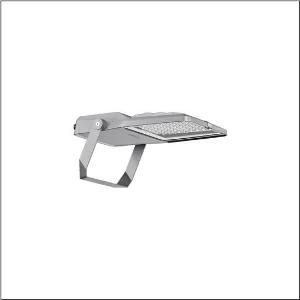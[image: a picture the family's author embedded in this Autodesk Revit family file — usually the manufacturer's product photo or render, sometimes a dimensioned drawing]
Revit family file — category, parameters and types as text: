
# Revit family: floodlight_fl_21_mini___pl64_5xa7776b2e1a_6c25
name_source: partatom
category: Lighting Fixtures
units: mm (PartAtom-declared; Revit-internal decimal feet)

## family parameters
Cut with Voids When Loaded = No
Host = Face
Light Source = No
Part Type = Normal
Room Calculation Point = No
Round Connector Dimension = Use Diameter
Shared = No

## types (1)
- --- (1 x LED, 6010 lm, 45.7 W, 3000K)
    Apparent Load = 46 VA
    CIE Flux Codes = 28 80 98 100 100
    Color Rendering = 70
    Color Temperature = 3000K
    Default Elevation = 1800 mm
    Description = Floodlight FL 21 mini, floodlight, primary light control with lens, of PMMA, primary optical cover: protective disc, of toughened safety glass, transparent, light distribution: PL64, light emission: direct distribution, installation type: surface-mounted, LED, High Power LED, rated luminous flux: 6.010lm, luminous efficacy: 132lm/W, light colour: 730, colour temperature: 3000K, control gear: Smart Interface (Zhaga), control: flexible luminous flux parameterisation, time-dependent luminous flux control, constant luminous flux control, overheat protection, pre-setting: logarithmic dimming characteristic, with terminal, 6-pole, mains connection: 220..240V, AC, 50/60Hz, start of lifetime: 46W, end of service life: 48W, reduction: 22W, luminaire housing, of diecast aluminium, powder-coated, SITECO metallic grey (DB 702S), corrosivity category C5 mid according to DIN EN ISO 12944, suitable for swimming pools, chlorine-resistant, sealing non-destructively replaceable, mounting bracket, of steel, galvanised, powder-coated, SITECO metallic grey (DB 702S), Smart Interface below and above, protection rating (complete): IP66, insulation class (complete): insulation class II (safety insulation), certification: CE, ENEC, VDE, protection symbol: D, impact resistance: IK08, permissible operating ambient temperature: -40..+40°C, permissible operating ambient temperature for outdoor applications: -40..+50°C, standard: DIN EN 12944, LABS conformity tested according to VDMA 24364:2018-05, packaging unit: 1 piece

Light Distribution: PL64
    Height = 70 mm
    Lamp = 1 x LED
    Lamp Light Flux = 6010 lm
    Lamp Power = 45.7 W
    Lamp count = 1
    Length = 485 mm
    Luminous efficacy = 132 lm/W
    Manufacturer = Siteco
    ModVariant = No
    Model = 5XA7776B2E1A
    Mounting Place = Pole
    Mounting Type = Pole annexe
    Number of Poles = 1
    OnlyDefault = Yes
    Power Factor = 1
    Product Name = Floodlight FL 21 mini | PL64
    Product group = floodlight | pylon annexe
    ProductGroupID = 6201
    Protection Class = Protection class II
    Protection Degree = IP 66
    RLX_Detail_Level = 1
    RLX_Emergency_Light_Flux = 0 lm
    RLX_Emergency_Type = 0
    RLX_Emergency_Type_DB = No
    RlxData = <blob elided: 96037 chars, md5=47f58346>
    Socket = socket
    Standby Power = 0 W
    System Light Flux = 6010 lm
    System Power = 46 W
    Type Comments = factory setting: luminous flux: 100 % | dim-lin: 254 | 463 mA
    Type Image = l_1006845.jpg
    URL = http://relux.com
    VarID = @adj_166543
    Voltage = 0 V
    Weight = 0.00 kg
    Width = 337 mm

## geometry (parser evidence)
native form markers: Blend x4, Sweep x13
no freeform markers — native parametric forms only
